# Revit family: ASH_Contour21_S6458_BIM_GB
name_source: partatom
category: Plumbing Fixtures
revit_build: Autodesk Revit MEP 2014 (Build: 20130308_1515(x64)
units: mm (PartAtom-declared; Revit-internal decimal feet)

## types (5) — shared parameters
AccessibilityPerformance = Part-M
Accessories = www.idealspec.co.uk
AreaUnits = millimeters
Assembly Code = C1030200
AssetType = Fixed
Brand = Armitage Shanks
ConnectionType = Plumbing
Default Elevation = 680 mm  [stored 2.23097 ft]
Description = Contour 21 grab rail straight 90cm long x 35mm diameter
DurationUnit = year
ExpectedLife = 30
Features = Grab rail straight 90cm long x 35mm diameter
Finish = Chrome
IfcExportAs = IfcValveType
IfcExportType = FAUCET
InstallationInstructions = www.idealspec.co.uk/resources.html
LinearUnits = millimeters
ManufacturerURL = www.idealspec.co.uk
Material = Aluminium
ModelReference = Contour 21 grab rail straight 90cm long x 35mm diameter
NBSDescription = Support rails
NBSReference = 45-35-70/360
NettWeight = 0.62 Kg
NominalHeight = 100 mm  [stored 0.328084 ft]
NominalLength = 900 mm  [stored 2.95276 ft]
Shape = Sculptured
Size = 0 x 0 x 0 mm
Space = Internal
SpareParts = www.fastpart-spares.co.uk
URL = www.idealspec.co.uk
Uniclass2015Code = Pr_40_20_76_84
Uniclass2015Title = Support rails
Uniclass2015Version = Products v1.1
Version = 1
VolumeUnits = Litres
WarrantyDescription = Manufacturers Warranty
WarrantyDurationParts = 5
WarrantyDurationUnit = year
zero-valued in all types: CWFU, Cost, HWFU, NominalWidth, WFU

## per-type parameters (varying)
| type | BIMObjectName | BarCode | Color | GrabRailMtl | Model | ModelNumber | Name | ProductInformation |
| S645836 - Contour21 Grab Rail 900mm Straight - Blue | ASH_ArmitageShanks_SupportRails_Contour21_S645836 | 5017830384922 | Blue | ASH_ArmitageShank_Brassware_Blue_36_Render | S645836 | S645836 | SupportRails_Contour21_S645836_ArmitageShanks | www.idealspec.co.uk/assets/datasheet/S645836 |
| S6458RN - Contour21 Grab Rail 900mm Straight - Charcoal | ASH_ArmitageShanks_SupportRails_Contour21_S6458RN | 5017830388463 | Charcoal | ASH_ArmitageShank_Brassware_Charcoal_RN_Render | S6458RN | S6458RN | SupportRails_Contour21_S6458RN_ArmitageShanks | www.idealspec.co.uk/assets/datasheet/S6458RN |
| S6458LJ - Contour21 Grab Rail 900mm Straight - Light Grey | ASH_ArmitageShanks_SupportRails_Contour21_S6458LJ | 5017830384601 | Grey | ASH_ArmitageShank_Brassware_Grey_LJ_Render | S6458LJ | S6458LJ | SupportRails_Contour21_S6458LJ_ArmitageShanks | www.idealspec.co.uk/assets/datasheet/S6458LJ |
| S6458MY - Contour21 Grab Rail 900mm Straight - Stainless Steel | ASH_ArmitageShanks_SupportRails_Contour21_S6458MY | 5017830384281 | Stainless Steel finish | ASH_ArmitageShank_Brassware_Steel_MY_Render | S6458MY | S6458MY | SupportRails_Contour21_S6458MY_ArmitageShanks | www.idealspec.co.uk/assets/datasheet/S6458MY |
| S6458AC - Contour21 Grab Rail 900mm Straight - White | ASH_ArmitageShanks_SupportRails_Contour21_S6458AC | 5017830383802 | White | ASH_ArmitageShank_Brassware_White_AC_Render | S6458AC | S6458AC | SupportRails_Contour21_S6458AC_ArmitageShanks | www.idealspec.co.uk/assets/datasheet/S6458AC |

note: [stored X ft] marks values corroborated as IEEE doubles in the binary element streams (Revit-internal decimal feet)

## geometry (parser evidence)
native form markers: Sweep x4
no freeform markers — native parametric forms only
